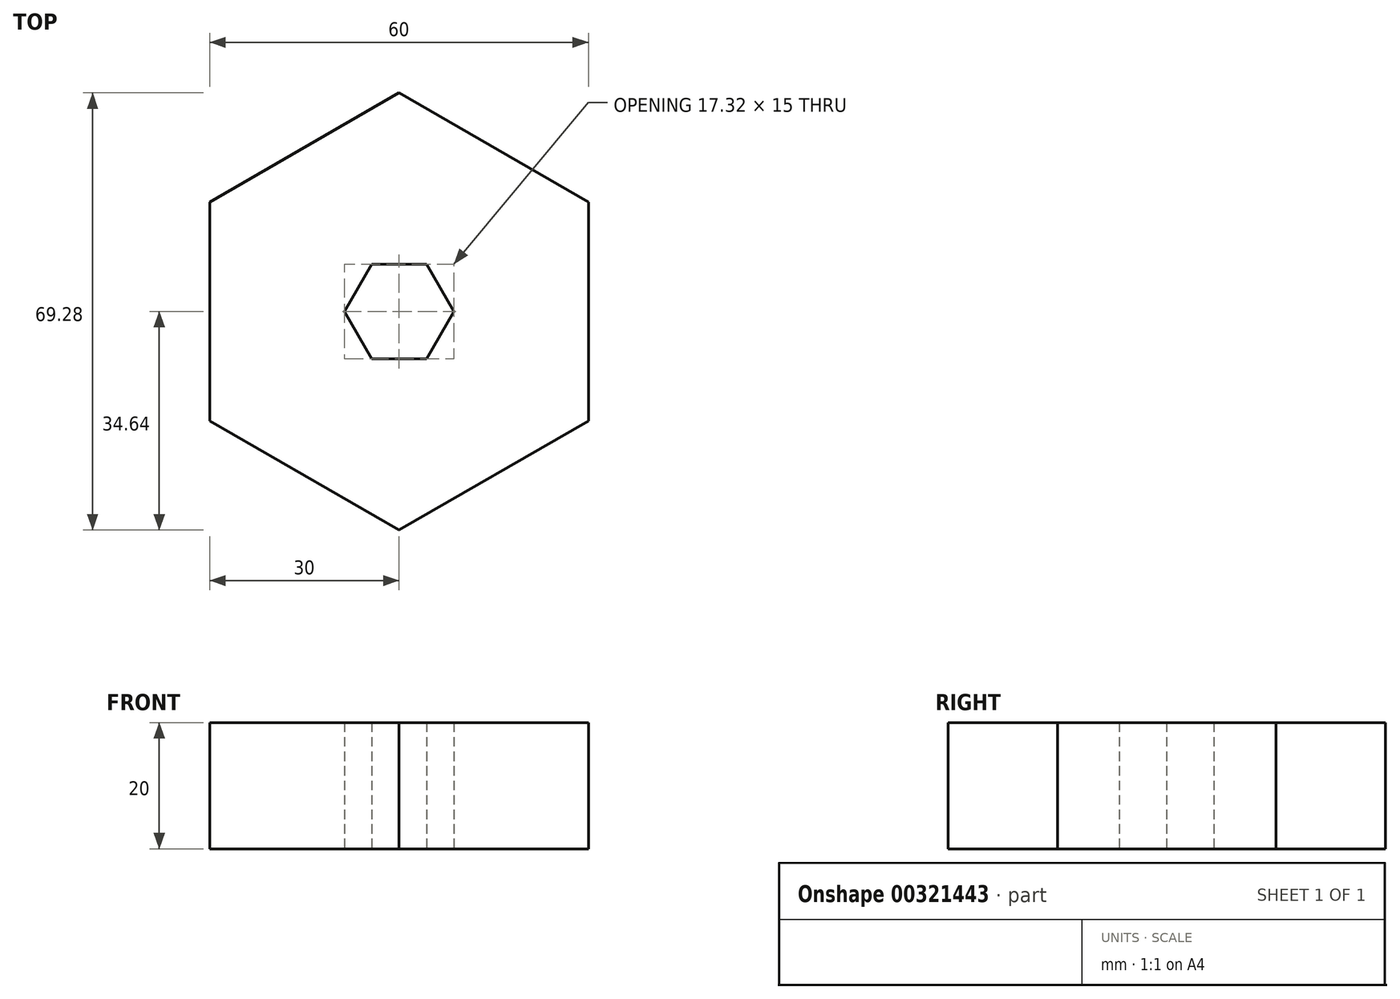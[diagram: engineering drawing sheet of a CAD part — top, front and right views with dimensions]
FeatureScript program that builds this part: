
annotation { "Feature Type Name" : "Feature", "Feature Type Description" : "" }
export const myFeature = defineFeature(function(context is Context, id is Id, definition is map)
    precondition{}
    {
        {
            var Q0;
            Q0=qCreatedBy(makeId("Top.planeOp"),FACE);
            var sketch = newSketch(context, id + "F0", { "sketchPlane" : qUnion([Q0])});
            skCircle(sketch, "E0.cCircle", {"center": v(0, 0) * mm, "radius": 34.64 * mm, "construction": true});
            skLineSegment(sketch, "E0.0", {"start": v(30, -17.32) * mm, "end": v(0, -34.64) * mm});
            skLineSegment(sketch, "E0.1", {"start": v(0, -34.64) * mm, "end": v(-30, -17.32) * mm});
            skLineSegment(sketch, "E0.2", {"start": v(-30, -17.32) * mm, "end": v(-30, 17.32) * mm});
            skLineSegment(sketch, "E0.3", {"start": v(-30, 17.32) * mm, "end": v(0, 34.64) * mm});
            skLineSegment(sketch, "E0.4", {"start": v(0, 34.64) * mm, "end": v(30, 17.32) * mm});
            skLineSegment(sketch, "E0.5", {"start": v(30, 17.32) * mm, "end": v(30, -17.32) * mm});
            skCircle(sketch, "E1.cCircle", {"center": v(0, 0) * mm, "radius": 7.5 * mm, "construction": true});
            skLineSegment(sketch, "E1.0", {"start": v(8.66, 0) * mm, "end": v(4.33, -7.5) * mm});
            skLineSegment(sketch, "E1.1", {"start": v(4.33, -7.5) * mm, "end": v(-4.33, -7.5) * mm});
            skLineSegment(sketch, "E1.2", {"start": v(-4.33, -7.5) * mm, "end": v(-8.66, 0) * mm});
            skLineSegment(sketch, "E1.3", {"start": v(-8.66, 0) * mm, "end": v(-4.33, 7.5) * mm});
            skLineSegment(sketch, "E1.4", {"start": v(-4.33, 7.5) * mm, "end": v(4.33, 7.5) * mm});
            skLineSegment(sketch, "E1.5", {"start": v(4.33, 7.5) * mm, "end": v(8.66, 0) * mm});
            skPoint(sketch, "E1.0.midPoint", {"position": v(6.5, -3.75) * mm});
            skSolve(sketch);
        }
        {
            var Q0;
            Q0 = qSketchRegion(id + "F0", true);
            extrude(context, id + "F1", {"entities" : qUnion([Q0]), "depth" : 20 * mm});
        }
    });
